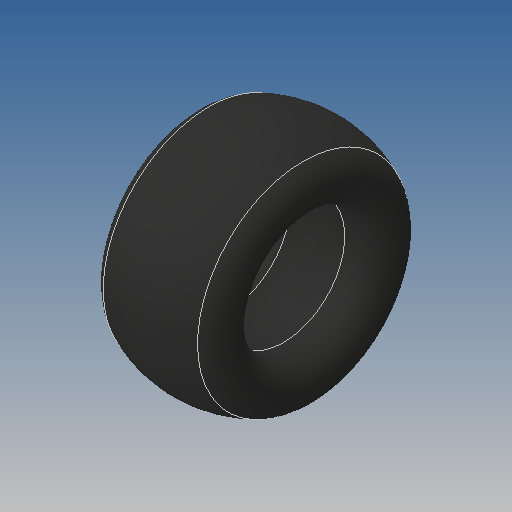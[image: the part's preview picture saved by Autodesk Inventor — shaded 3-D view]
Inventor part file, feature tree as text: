
AUTODESK INVENTOR PART (.ipt)
format: ipt  version: 2020 (Build 240168000, 168)  size: 196,608 bytes
history: native  units: mm
features: sketch x2, other x1, sweep x1
ambient origin geometry x8: Origin, YZ Plane, XZ Plane, XY Plane, X Axis, Y Axis, Z Axis, Center Point
bodies: Body1 (feature_tree)
feature tree (4):
  other  "Твердое тело1"
  sweep  "Сдвиг1"
  sketch  "Эскиз1"
  sketch  "Эскиз2"
